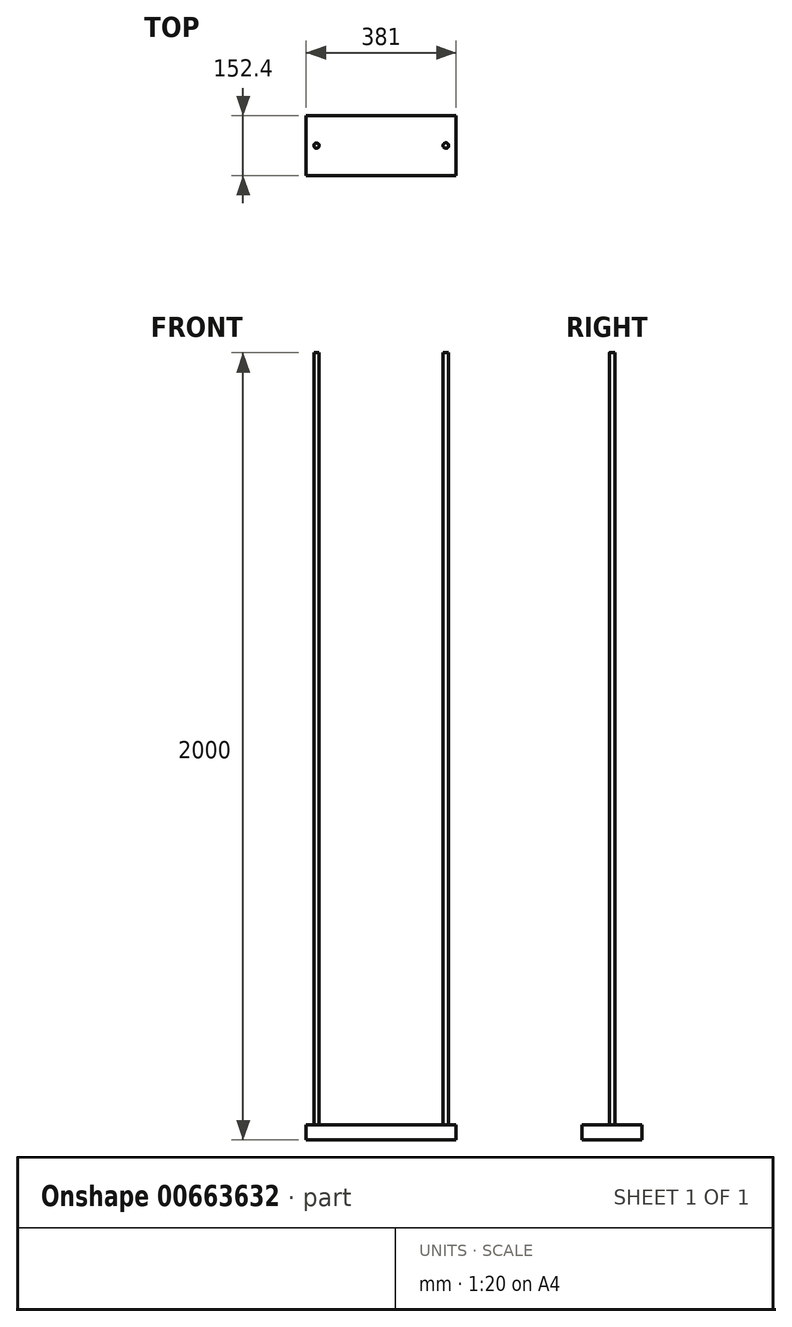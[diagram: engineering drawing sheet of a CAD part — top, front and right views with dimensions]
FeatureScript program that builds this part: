
annotation { "Feature Type Name" : "Feature", "Feature Type Description" : "" }
export const myFeature = defineFeature(function(context is Context, id is Id, definition is map)
    precondition{}
    {
        {
            var Q0;
            Q0=qCreatedBy(makeId("Top.planeOp"),FACE);
            var sketch = newSketch(context, id + "F0", { "sketchPlane" : qUnion([Q0])});
            skLineSegment(sketch, "E0.bottom", {"start": v(190.5, -76.2) * mm, "end": v(-190.5, -76.2) * mm});
            skLineSegment(sketch, "E0.top", {"start": v(190.5, 76.2) * mm, "end": v(-190.5, 76.2) * mm});
            skLineSegment(sketch, "E0.left", {"start": v(190.5, -76.2) * mm, "end": v(190.5, 76.2) * mm});
            skLineSegment(sketch, "E0.right", {"start": v(-190.5, -76.2) * mm, "end": v(-190.5, 76.2) * mm});
            skPoint(sketch, "E0.middle", {"position": v(0, 0) * mm});
            skSolve(sketch);
        }
        {
            var Q0;
            Q0=makeQuery(id+"F0.imprint","IMPRINT",FACE,{"disambiguationData":[TD([[makeQuery(id+"F0.imprint","IMPRINT",EDGE,{"derivedFrom":sQuery(id+"F0.wireOp",EDGE,"E0.bottom")}),-1.0]])]});
            extrude(context, id + "F1", {"entities" : qUnion([Q0]), "depth" : 38.1 * mm, "offsetDistance" : 25.4 * mm});
        }
        {
            var Q0;
            Q0=qCreatedBy(makeId("Top.planeOp"),FACE);
            var sketch = newSketch(context, id + "F2", { "sketchPlane" : qUnion([Q0])});
            skCircle(sketch, "E1", {"center": v(-164.24, 0) * mm, "radius": 6.73 * mm});
            skSolve(sketch);
        }
        {
            var Q0;
            Q0=qCreatedBy(makeId("Top.planeOp"),FACE);
            var sketch = newSketch(context, id + "F3", { "sketchPlane" : qUnion([Q0])});
            skCircle(sketch, "E2", {"center": v(164.53, 0) * mm, "radius": 7.09 * mm});
            skSolve(sketch);
        }
        {
            var Q0;
            Q0 = qSketchRegion(id + "F2", true);
            extrude(context, id + "F4", {"entities" : qUnion([Q0]), "operationType" : NewBodyOperationType.ADD, "depth" : 2000 * mm, "offsetDistance" : 25.4 * mm});
        }
        {
            var Q0;
            Q0 = qSketchRegion(id + "F3", true);
            extrude(context, id + "F5", {"entities" : qUnion([Q0]), "operationType" : NewBodyOperationType.ADD, "depth" : 2000 * mm, "offsetDistance" : 25.4 * mm});
        }
    });
